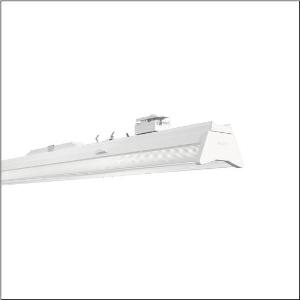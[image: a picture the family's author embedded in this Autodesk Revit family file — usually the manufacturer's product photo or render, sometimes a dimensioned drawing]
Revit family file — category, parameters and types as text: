
# Revit family: licross_r__11_performance_ho_51td16dn4fxm_21ba
name_source: partatom
category: Lighting Fixtures
units: mm (PartAtom-declared; Revit-internal decimal feet)

## family parameters
Cut with Voids When Loaded = No
Host = Face
Light Source = No
Part Type = Normal
Room Calculation Point = No
Round Connector Dimension = Use Diameter
Shared = No

## types (1)
- --- (1 x LED, 15460 lm, 87.3 W, 4000K)
    Apparent Load = 87 VA
    CIE Flux Codes = 63 87 95 78 100
    Color Rendering = 80
    Color Temperature = 4000K
    Default Elevation = 1800 mm
    Description = Licross® 11 Performance HO, luminaire insert, of sheet steel, galvanised, coil coated, white, length: 1.500mm, width: 120mm, height: 123mm, LED rated luminous flux: 15.460lm, light colour: 840, control gear: DALI 2, with plug, 5-pole, with phase selection, mains connection: 220..240V, AC, 50/60Hz, rated input power: 87W, halogen-free wiring, primary light control with lens, of plastic, primary optical cover: cover, of PMMA, light emission: direct/indirect distribution, primary light characteristic: symmetric, protection rating (complete): IP54, insulation class (complete): insulation class I (protective earthing), certification: CE, ENEC, VDE, UKCA, protection symbol: D if used in an environment with non-conductive dust loads with corresponding accessories, impact resistance: IK06, permissible ambient temperature for indoor applications: -25..+30°C, corresponds to IFS (International Featured Standards) requirements for safety and quality in the food industry, reducing of maximum allowable ambient temperature of 5°C with ceiling mounting, LABS conformity tested according to VDMA 24364:2018-05, packaging unit: 1 piece
    Height = 114 mm
    Lamp = 1 x LED
    Lamp Light Flux = 15460 lm
    Lamp Power = 87.3 W
    Lamp count = 1
    Length = 1500 mm
    Luminous efficacy = 177 lm/W
    Manufacturer = Siteco
    ModVariant = No
    Model = 51TD16DN4FXM
    Mounting Place = Ceiling
    Mounting Type = Pendant
    Number of Poles = 1
    OnlyDefault = Yes
    Power Factor = 1
    Product Name = Licross® 11 Performance HO
    Product group = luminaire insert
    ProductGroupID = 901
    Protection Class = Protection class I
    Protection Degree = IP 54
    RLX_Detail_Level = 1
    RLX_Emergency_Light_Flux = 0 lm
    RLX_Emergency_Type = 0
    RLX_Emergency_Type_DB = No
    RlxData = <blob elided: 34049 chars, md5=c46067cb>
    Socket = socket
    Standby Power = 0 W
    System Light Flux = 15460 lm
    System Power = 87 W
    Type Comments = factory setting: luminous flux: 100 % | dim-lin: 254 | 589 mA
    Type Image = l_1256138.jpg
    URL = http://relux.com
    VarID = @adj_070239
    Voltage = 0 V
    Weight = 0.00 kg
    Width = 120 mm

## geometry (parser evidence)
native form markers: Blend x4, Sweep x11
no freeform markers — native parametric forms only
